# Revit family: Taza TZF NAO17
name_source: partatom
category: Aparatos sanitarios
revit_build: Autodesk Revit 2016 (Build: 20150220_1215(x64)
units: mm (PartAtom-declared; Revit-internal decimal feet)

## family parameters
Compartido = Sí
Corte con vacíos al cargar = No
Cota de conector redondo = Diámetro de uso
Número OmniClass = 23.45.05.14.31
Punto de cálculo de habitación = Sí
Se basa en plano de trabajo = Sí
Siempre vertical = Sí
Tipo de pieza = Normal
Título OmniClass = Combination Toilets

## types (2) — shared parameters
Certification = http://www.helvex.com.mx
Comentarios de tipo = Ceramic
Compliance = NOM-009-CONAGUA-2001; ASME A112.19.2-2008; CSA B45.1-08
Data Sheet = http://www.helvex.com.mx
Descripción = 1,26 gpf Nao Flush Toilet With Exposed Trapway And Comfortable Height
Fabricante = HELVEX
Features = Sleek Ergonomic Design; Flat Base; Sturdy Built; Premium Quality High Gloss (A); Exposed Glazed Trapway; Siphon Action Jetted Bowl; Optimum Water Surface; Requires 1,26 gpf Flushvalve; Includes Setting Kit; Saves On Water Consumption; 17" Comfortable Height
High Gloss Ceramic = High Gloss Ceramic
Inlet Threads = Feeding: 15/16" - 14 NS - 1; Flush: Coupled With Sanitary Flange
Instructive = http://www.helvex.com.mx
Max. Working Pressure = 85.3 psi
Maximum Consumption = 1,26 gpf
Min. Working Pressure = 14.2 psi
Total Height = 17"
Total Length = 26"
Total Width = 15"
URL = http://www.helvex.com.mx

## per-type parameters (varying)
| type | Elevación por defecto | Imagen de tipo |
| TZF-17 | 48" | <Ninguno> |
| TZF NAO17 | 4" | TZF NAO17.jpg |

note: column(s) folded — value = type name in every type: Modelo

## geometry (parser evidence)
native form markers: Blend x4, Sweep x3
no freeform markers — native parametric forms only
